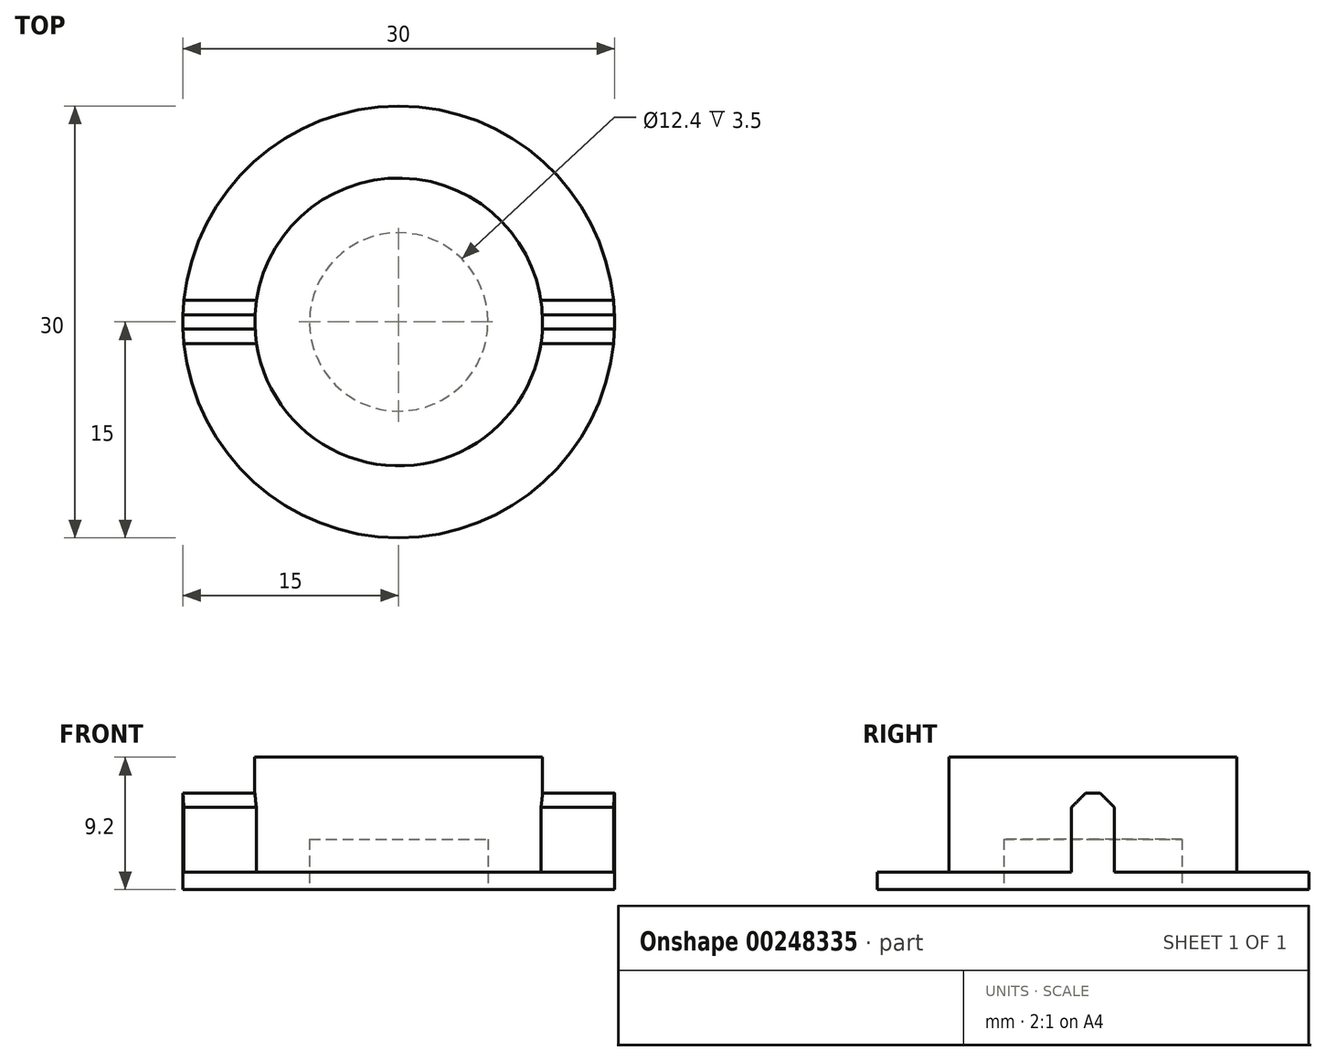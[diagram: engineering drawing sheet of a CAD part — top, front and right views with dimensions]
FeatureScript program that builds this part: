
annotation { "Feature Type Name" : "Feature", "Feature Type Description" : "" }
export const myFeature = defineFeature(function(context is Context, id is Id, definition is map)
    precondition{}
    {
        {
            var Q0;
            Q0=qCreatedBy(makeId("Top.planeOp"),FACE);
            var sketch = newSketch(context, id + "F0", { "sketchPlane" : qUnion([Q0])});
            skCircle(sketch, "E0", {"center": v(0, 0) * mm, "radius": 10 * mm});
            skSolve(sketch);
        }
        {
            var Q0;
            Q0 = qSketchRegion(id + "F0", true);
            extrude(context, id + "F1", {"entities" : qUnion([Q0]), "depth" : 8 * mm});
        }
        {
            var Q0;
            Q0=makeQuery(id+"F1.opExtrude","CAP_FACE",FACE,{"disambiguationData":[OSD([sQuery(id+"F0.wireOp",EDGE,"E0")])],"isStart":true});
            var sketch = newSketch(context, id + "F2", { "sketchPlane" : qUnion([Q0])});
            skCircle(sketch, "E1", {"center": v(0, 0) * mm, "radius": 15 * mm});
            skSolve(sketch);
        }
        {
            var Q0;
            Q0 = qSketchRegion(id + "F2", true);
            extrude(context, id + "F3", {"entities" : qUnion([Q0]), "operationType" : NewBodyOperationType.ADD, "depth" : 1.2 * mm});
        }
        {
            var Q0;
            Q0=makeQuery(id+"F3.opExtrude","CAP_FACE",FACE,{"disambiguationData":[OSD([sQuery(id+"F2.wireOp",EDGE,"E1")])],"isStart":false});
            var sketch = newSketch(context, id + "F4", { "sketchPlane" : qUnion([Q0])});
            skCircle(sketch, "E2", {"center": v(0, 0) * mm, "radius": 6.2 * mm});
            skSolve(sketch);
        }
        {
            var Q0;
            Q0 = qSketchRegion(id + "F4", true);
            extrude(context, id + "F5", {"entities" : qUnion([Q0]), "operationType" : NewBodyOperationType.REMOVE, "oppositeDirection" : true, "depth" : 3.5 * mm});
        }
        {
            var Q0;
            Q0=makeQuery(id+"F3.opExtrude","CAP_FACE",FACE,{"disambiguationData":[OSD([sQuery(id+"F2.wireOp",EDGE,"E1")])],"isStart":true});
            var sketch = newSketch(context, id + "F6", { "sketchPlane" : qUnion([Q0])});
            skLineSegment(sketch, "E3.bottom", {"start": v(17.5, -1.5) * mm, "end": v(-17.5, -1.5) * mm});
            skLineSegment(sketch, "E3.top", {"start": v(17.5, 1.5) * mm, "end": v(-17.5, 1.5) * mm});
            skLineSegment(sketch, "E3.left", {"start": v(17.5, -1.5) * mm, "end": v(17.5, 1.5) * mm});
            skLineSegment(sketch, "E3.right", {"start": v(-17.5, -1.5) * mm, "end": v(-17.5, 1.5) * mm});
            skPoint(sketch, "E3.middle", {"position": v(0, 0) * mm});
            skCircle(sketch, "E4.0", {"center": v(0, 0) * mm, "radius": 15 * mm});
            skSolve(sketch);
        }
        {
            var Q0;
            {var subQ0=sQuery(id+"F6.wireOp",EDGE,"E4.0");var subQ1=sQuery(id+"F6.wireOp",EDGE,"E3.bottom");var subQ2=makeQuery(id+"F6.imprint","INTERSECT",VERTEX,{"disambiguationData":[OD(1.0)],"derivedFrom":[subQ1,subQ0]});Q0=makeQuery(id+"F6.imprint","IMPRINT",FACE,{"disambiguationData":[TD([[makeQuery(id+"F6.imprint","IMPRINT",EDGE,{"disambiguationData":[TD([[subQ2,1.0]])],"derivedFrom":subQ1}),-1.0]])]});}
            var Q1;
            {var subQ0=sQuery(id+"F6.wireOp",EDGE,"E4.0");var subQ1=sQuery(id+"F6.wireOp",EDGE,"E3.bottom");var subQ2=makeQuery(id+"F6.imprint","INTERSECT",VERTEX,{"disambiguationData":[OD(0.0)],"derivedFrom":[subQ1,subQ0]});Q1=makeQuery(id+"F6.imprint","IMPRINT",FACE,{"disambiguationData":[TD([[makeQuery(id+"F6.imprint","IMPRINT",EDGE,{"disambiguationData":[TD([[subQ2,-1.0]])],"derivedFrom":subQ1}),-1.0]])]});}
            extrude(context, id + "F7", {"entities" : qUnion([Q0, Q1]), "operationType" : NewBodyOperationType.ADD, "depth" : 5.5 * mm});
        }
        {
            var Q0;
            {var subQ0=sQuery(id+"F6.wireOp",EDGE,"E3.bottom");Q0=makeQuery(id+"F7.opExtrude","CAP_EDGE",EDGE,{"disambiguationData":[OSD([subQ0]),TDD([makeQuery(id+"F6.imprint","IMPRINT",EDGE,{"disambiguationData":[TD([[makeQuery(id+"F6.imprint","INTERSECT",VERTEX,{"disambiguationData":[OD(1.0)],"derivedFrom":[subQ0,sQuery(id+"F6.wireOp",EDGE,"E4.0")]}),1.0]])],"derivedFrom":subQ0})])],"isStart":false});}
            var Q1;
            {var subQ0=sQuery(id+"F6.wireOp",EDGE,"E3.top");Q1=makeQuery(id+"F7.opExtrude","CAP_EDGE",EDGE,{"disambiguationData":[OSD([subQ0]),TDD([makeQuery(id+"F6.imprint","IMPRINT",EDGE,{"disambiguationData":[TD([[makeQuery(id+"F6.imprint","INTERSECT",VERTEX,{"disambiguationData":[OD(1.0)],"derivedFrom":[subQ0,sQuery(id+"F6.wireOp",EDGE,"E4.0")]}),1.0]])],"derivedFrom":subQ0})])],"isStart":false});}
            var Q2;
            {var subQ0=sQuery(id+"F6.wireOp",EDGE,"E3.top");Q2=makeQuery(id+"F7.opExtrude","CAP_EDGE",EDGE,{"disambiguationData":[OSD([subQ0]),TDD([makeQuery(id+"F6.imprint","IMPRINT",EDGE,{"disambiguationData":[TD([[makeQuery(id+"F6.imprint","INTERSECT",VERTEX,{"disambiguationData":[OD(0.0)],"derivedFrom":[subQ0,sQuery(id+"F6.wireOp",EDGE,"E4.0")]}),-1.0]])],"derivedFrom":subQ0})])],"isStart":false});}
            var Q3;
            {var subQ0=sQuery(id+"F6.wireOp",EDGE,"E3.bottom");Q3=makeQuery(id+"F7.opExtrude","CAP_EDGE",EDGE,{"disambiguationData":[OSD([subQ0]),TDD([makeQuery(id+"F6.imprint","IMPRINT",EDGE,{"disambiguationData":[TD([[makeQuery(id+"F6.imprint","INTERSECT",VERTEX,{"disambiguationData":[OD(0.0)],"derivedFrom":[subQ0,sQuery(id+"F6.wireOp",EDGE,"E4.0")]}),-1.0]])],"derivedFrom":subQ0})])],"isStart":false});}
            chamfer(context, id + "F8", {"entities" : qUnion([Q0, Q1, Q2, Q3]), "width" : 1 * mm, "tangentPropagation" : true});
        }
    });
